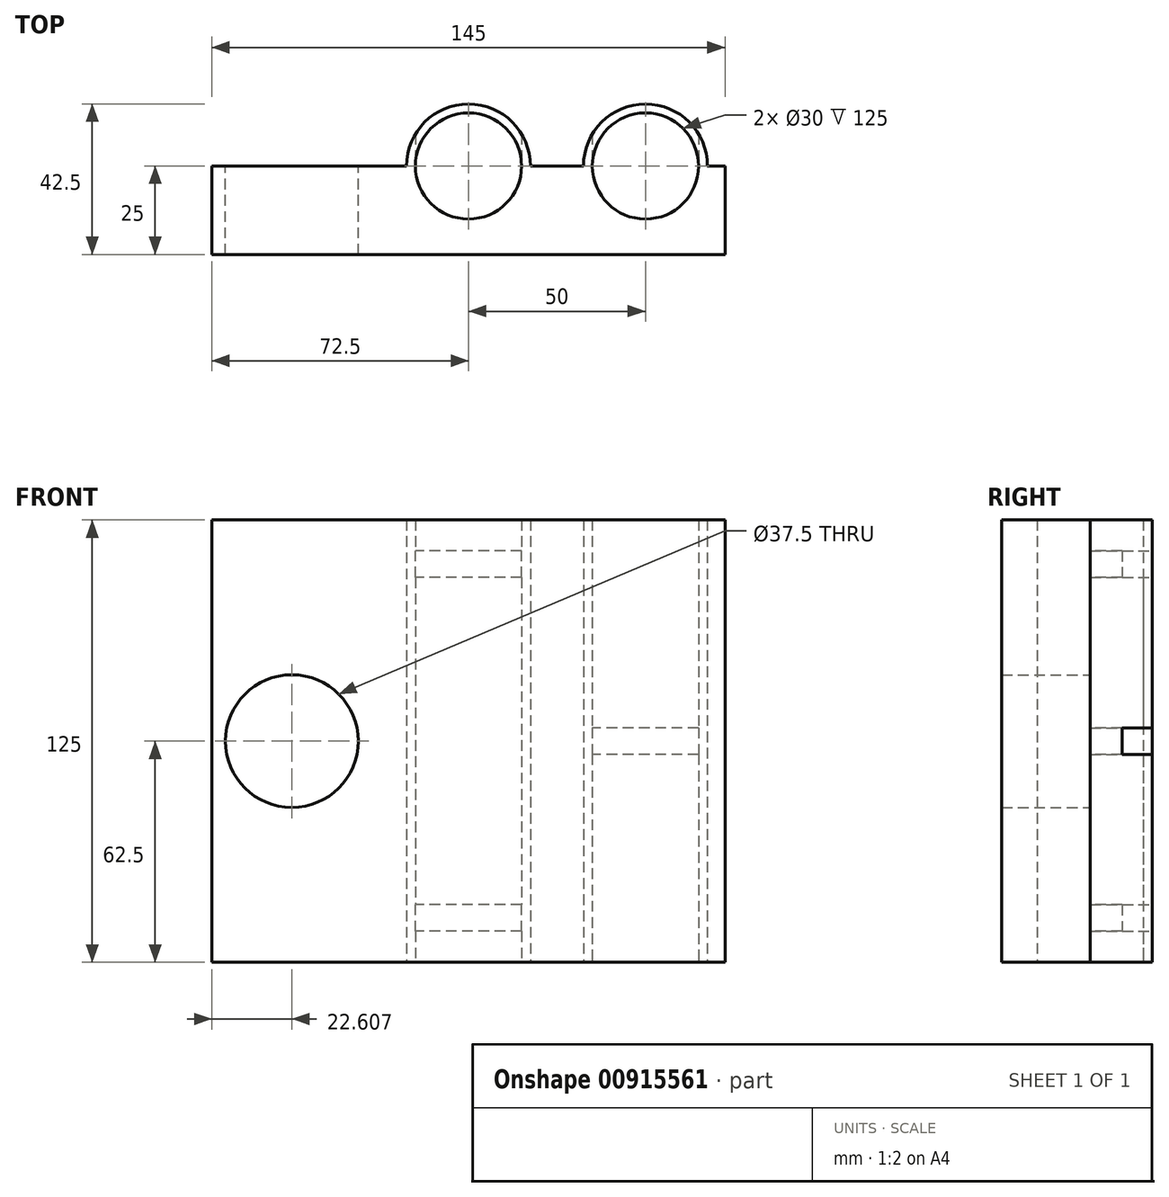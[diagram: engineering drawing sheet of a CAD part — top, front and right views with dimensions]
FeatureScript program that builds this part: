
annotation { "Feature Type Name" : "Feature", "Feature Type Description" : "" }
export const myFeature = defineFeature(function(context is Context, id is Id, definition is map)
    precondition{}
    {
        {
            var Q0;
            Q0=qCreatedBy(makeId("Front.planeOp"),FACE);
            var sketch = newSketch(context, id + "F0", { "sketchPlane" : qUnion([Q0])});
            skLineSegment(sketch, "E0.bottom", {"start": v(-72.5, 62.5) * mm, "end": v(72.5, 62.5) * mm});
            skLineSegment(sketch, "E0.top", {"start": v(-72.5, -62.5) * mm, "end": v(72.5, -62.5) * mm});
            skLineSegment(sketch, "E0.left", {"start": v(-72.5, 62.5) * mm, "end": v(-72.5, -62.5) * mm});
            skLineSegment(sketch, "E0.right", {"start": v(72.5, 62.5) * mm, "end": v(72.5, -62.5) * mm});
            skPoint(sketch, "E0.middle", {"position": v(0, 0) * mm});
            skSolve(sketch);
        }
        {
            var Q0;
            Q0=makeQuery(id+"F0.imprint","IMPRINT",FACE,{"disambiguationData":[TD([[makeQuery(id+"F0.imprint","IMPRINT",EDGE,{"derivedFrom":sQuery(id+"F0.wireOp",EDGE,"E0.bottom")}),-1.0]])]});
            extrude(context, id + "F1", {"entities" : qUnion([Q0]), "depth" : 25 * mm, "offsetDistance" : 25 * mm});
        }
        {
            var Q0;
            Q0=makeQuery(id+"F1.opExtrude","CAP_FACE",FACE,{"disambiguationData":[OSD([sQuery(id+"F0.wireOp",EDGE,"E0.bottom"),sQuery(id+"F0.wireOp",EDGE,"E0.top"),sQuery(id+"F0.wireOp",EDGE,"E0.left"),sQuery(id+"F0.wireOp",EDGE,"E0.right")])],"isStart":true});
            var sketch = newSketch(context, id + "F2", { "sketchPlane" : qUnion([Q0])});
            skLineSegment(sketch, "E1.bottom", {"start": v(-15, 46.25) * mm, "end": v(15, 46.25) * mm});
            skLineSegment(sketch, "E1.top", {"start": v(-15, 53.75) * mm, "end": v(15, 53.75) * mm});
            skLineSegment(sketch, "E1.left", {"start": v(-15, 46.25) * mm, "end": v(-15, 53.75) * mm});
            skLineSegment(sketch, "E1.right", {"start": v(15, 46.25) * mm, "end": v(15, 53.75) * mm});
            skPoint(sketch, "E1.middle", {"position": v(0, 50) * mm});
            skLineSegment(sketch, "E2.bottom", {"start": v(-15, -53.75) * mm, "end": v(15, -53.75) * mm});
            skLineSegment(sketch, "E2.top", {"start": v(-15, -46.25) * mm, "end": v(15, -46.25) * mm});
            skLineSegment(sketch, "E2.left", {"start": v(-15, -53.75) * mm, "end": v(-15, -46.25) * mm});
            skLineSegment(sketch, "E2.right", {"start": v(15, -53.75) * mm, "end": v(15, -46.25) * mm});
            skPoint(sketch, "E2.middle", {"position": v(0, -50) * mm});
            skLineSegment(sketch, "E3.bottom", {"start": v(-65, 3.75) * mm, "end": v(-35, 3.75) * mm});
            skLineSegment(sketch, "E3.top", {"start": v(-65, -3.75) * mm, "end": v(-35, -3.75) * mm});
            skLineSegment(sketch, "E3.left", {"start": v(-65, 3.75) * mm, "end": v(-65, -3.75) * mm});
            skLineSegment(sketch, "E3.right", {"start": v(-35, 3.75) * mm, "end": v(-35, -3.75) * mm});
            skPoint(sketch, "E3.middle", {"position": v(-50, 0) * mm});
            skCircle(sketch, "E4", {"center": v(49.9, 0) * mm, "radius": 18.75 * mm});
            skSolve(sketch);
        }
        {
            var Q0;
            Q0=qCreatedBy(makeId("Top.planeOp"),FACE);
            var sketch = newSketch(context, id + "F3", { "sketchPlane" : qUnion([Q0])});
            skCircle(sketch, "E5", {"center": v(0, 0) * mm, "radius": 15 * mm});
            skCircle(sketch, "E6", {"center": v(0, 0) * mm, "radius": 17.5 * mm});
            skCircle(sketch, "E7", {"center": v(50, 0) * mm, "radius": 15 * mm});
            skCircle(sketch, "E8", {"center": v(50, 0) * mm, "radius": 17.5 * mm});
            skSolve(sketch);
        }
        {
            var Q0;
            Q0=makeQuery(id+"F3.imprint","IMPRINT",FACE,{"disambiguationData":[TD([[makeQuery(id+"F3.imprint","IMPRINT",EDGE,{"derivedFrom":sQuery(id+"F3.wireOp",EDGE,"E5")}),-1.0]])]});
            var Q1;
            Q1=makeQuery(id+"F3.imprint","IMPRINT",FACE,{"disambiguationData":[TD([[makeQuery(id+"F3.imprint","IMPRINT",EDGE,{"derivedFrom":sQuery(id+"F3.wireOp",EDGE,"E7")}),-1.0]])]});
            extrude(context, id + "F4", {"entities" : qUnion([Q0, Q1]), "operationType" : NewBodyOperationType.ADD, "endBound" : BoundingType.SYMMETRIC, "depth" : 125 * mm, "offsetDistance" : 25 * mm});
        }
        {
            var Q0;
            Q0=makeQuery(id+"F2.imprint","IMPRINT",FACE,{"disambiguationData":[TD([[makeQuery(id+"F2.imprint","IMPRINT",EDGE,{"derivedFrom":sQuery(id+"F2.wireOp",EDGE,"E1.bottom")}),1.0]])]});
            var Q1;
            Q1=makeQuery(id+"F2.imprint","IMPRINT",FACE,{"disambiguationData":[TD([[makeQuery(id+"F2.imprint","IMPRINT",EDGE,{"derivedFrom":sQuery(id+"F2.wireOp",EDGE,"E2.bottom")}),1.0]])]});
            extrude(context, id + "F5", {"entities" : qUnion([Q0, Q1]), "operationType" : NewBodyOperationType.REMOVE, "depth" : 25 * mm, "offsetDistance" : 25 * mm});
        }
        {
            var Q0;
            Q0=makeQuery(id+"F2.imprint","IMPRINT",FACE,{"disambiguationData":[TD([[makeQuery(id+"F2.imprint","IMPRINT",EDGE,{"derivedFrom":sQuery(id+"F2.wireOp",EDGE,"E3.bottom")}),-1.0]])]});
            extrude(context, id + "F6", {"entities" : qUnion([Q0]), "operationType" : NewBodyOperationType.REMOVE, "depth" : 25 * mm, "offsetDistance" : 25 * mm});
        }
        {
            var Q0;
            Q0=makeQuery(id+"F2.imprint","IMPRINT",FACE,{"disambiguationData":[TD([[makeQuery(id+"F2.imprint","IMPRINT",EDGE,{"derivedFrom":sQuery(id+"F2.wireOp",EDGE,"E4")}),1.0]])]});
            extrude(context, id + "F7", {"entities" : qUnion([Q0]), "operationType" : NewBodyOperationType.REMOVE, "oppositeDirection" : true, "depth" : 2000 * mm, "offsetDistance" : 25 * mm});
        }
        {
            var Q0;
            Q0=makeQuery(id+"F3.imprint","IMPRINT",FACE,{"disambiguationData":[TD([[makeQuery(id+"F3.imprint","IMPRINT",EDGE,{"derivedFrom":sQuery(id+"F3.wireOp",EDGE,"E7")}),1.0]])]});
            var Q1;
            Q1=makeQuery(id+"F3.imprint","IMPRINT",FACE,{"disambiguationData":[TD([[makeQuery(id+"F3.imprint","IMPRINT",EDGE,{"derivedFrom":sQuery(id+"F3.wireOp",EDGE,"E5")}),1.0]])]});
            extrude(context, id + "F8", {"entities" : qUnion([Q0, Q1]), "operationType" : NewBodyOperationType.REMOVE, "endBound" : BoundingType.SYMMETRIC, "depth" : 25000 * mm, "offsetDistance" : 25 * mm});
        }
    });
